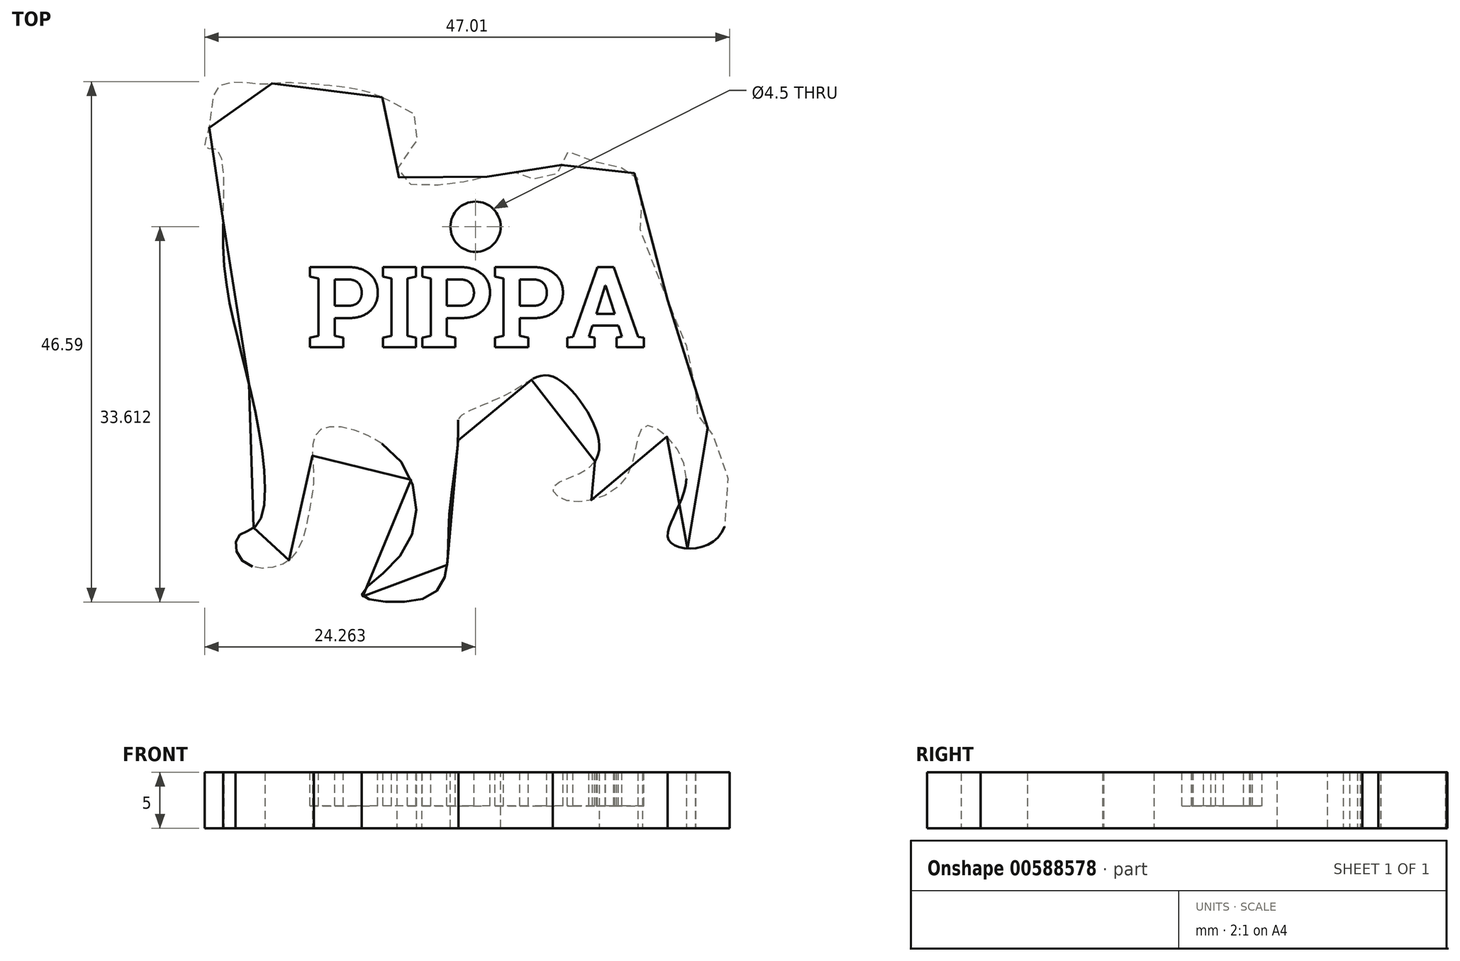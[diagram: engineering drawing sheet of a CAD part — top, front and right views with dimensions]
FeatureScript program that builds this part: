
annotation { "Feature Type Name" : "Feature", "Feature Type Description" : "" }
export const myFeature = defineFeature(function(context is Context, id is Id, definition is map)
    precondition{}
    {
        {
            var Q0;
            Q0=qCreatedBy(makeId("Top.planeOp"),FACE);
            var sketch = newSketch(context, id + "F0", { "sketchPlane" : qUnion([Q0])});
            skFitSpline(sketch, "E0", {"points": [v(-39.94, 54.57) * mm, v(-36.4, 51.95) * mm, v(-38.63, 48.03) * mm, v(-37.19, 46.72) * mm, v(-33.92, 46.85) * mm, v(-31.3, 47.24) * mm, v(-28.29, 47.9) * mm, v(-26.85, 47.37) * mm, v(-24.36, 47.63) * mm, v(-23.18, 49.73) * mm, v(-19.39, 48.16) * mm, v(-17.95, 48.29) * mm, v(-16.64, 45.8) * mm, v(-17.03, 43.7) * mm, v(-12.06, 30.1) * mm, v(-11.8, 26.3) * mm, v(-9.96, 23.68) * mm, v(-9.96, 15.04) * mm, v(-14.28, 14.91) * mm, v(-12.71, 20.8) * mm, v(-16.38, 25.12) * mm, v(-18.08, 20.54) * mm, v(-23.45, 18.44) * mm, v(-24.62, 19.62) * mm, v(-21.88, 21.06) * mm, v(-20.57, 23.94) * mm, v(-24.76, 29.57) * mm, v(-28.42, 28.13) * mm, v(-33, 25.9) * mm, v(-33.13, 24.6) * mm, v(-33.92, 17.4) * mm, v(-34.05, 13.6) * mm, v(-35.23, 10.2) * mm, v(-39.94, 9.41) * mm, v(-41.77, 10.07) * mm, v(-37.98, 14) * mm, v(-38.63, 22.37) * mm, v(-45.57, 24.73) * mm, v(-46.1, 20.93) * mm, v(-46.48, 17.53) * mm, v(-48.32, 13.08) * mm, v(-52.37, 12.95) * mm, v(-52.9, 15.17) * mm, v(-51.2, 16.22) * mm, v(-50.67, 22.63) * mm, v(-52.77, 32.45) * mm, v(-54.2, 41.74) * mm, v(-54.73, 49.86) * mm, v(-55.78, 49.99) * mm, v(-55.38, 52.08) * mm, v(-54.47, 55.62) * mm, v(-50.8, 55.75) * mm, v(-49.1, 55.88) * mm, v(-42.56, 55.36) * mm, v(-39.94, 54.57) * mm]});
            skSolve(sketch);
        }
        {
            var Q0;
            Q0=makeQuery(id+"F0.imprint","IMPRINT",FACE,{"disambiguationData":[TD([[makeQuery(id+"F0.imprint","IMPRINT",EDGE,{"derivedFrom":sQuery(id+"F0.wireOp",EDGE,"E0")}),-1.0]])]});
            extrude(context, id + "F1", {"entities" : qUnion([Q0]), "depth" : 5 * mm, "offsetDistance" : 25 * mm});
        }
        {
            var Q0;
            Q0=makeQuery(id+"F1.opExtrude","CAP_FACE",FACE,{"disambiguationData":[OSD([sQuery(id+"F0.wireOp",EDGE,"E0")])],"isStart":false});
            var sketch = newSketch(context, id + "F2", { "sketchPlane" : qUnion([Q0])});
            skCircle(sketch, "E1", {"center": v(-31.59, 42.96) * mm, "radius": 2.25 * mm});
            skSolve(sketch);
        }
        {
            var Q0;
            Q0 = qSketchRegion(id + "F2", true);
            extrude(context, id + "F3", {"entities" : qUnion([Q0]), "operationType" : NewBodyOperationType.REMOVE, "oppositeDirection" : true, "depth" : 5 * mm, "offsetDistance" : 25 * mm});
        }
        {
            var Q0;
            Q0=makeQuery(id+"F1.opExtrude","CAP_FACE",FACE,{"disambiguationData":[OSD([sQuery(id+"F0.wireOp",EDGE,"E0")])],"isStart":false});
            var sketch = newSketch(context, id + "F4", { "sketchPlane" : qUnion([Q0])});
            skText(sketch, "E2", { "text": "PIPPA\n\n", "fontName": "RobotoSlab-Bold.ttf"});
            const initialGuessF4  = {"E2": [-0.04669, 0.03217, 1, 0, 0.00727]};
            skSetInitialGuess(sketch, initialGuessF4);
            skSolve(sketch);
        }
        {
            var Q0;
            Q0 = qSketchRegion(id + "F4", true);
            extrude(context, id + "F5", {"entities" : qUnion([Q0]), "operationType" : NewBodyOperationType.REMOVE, "oppositeDirection" : true, "depth" : 3 * mm, "offsetDistance" : 25 * mm});
        }
    });
